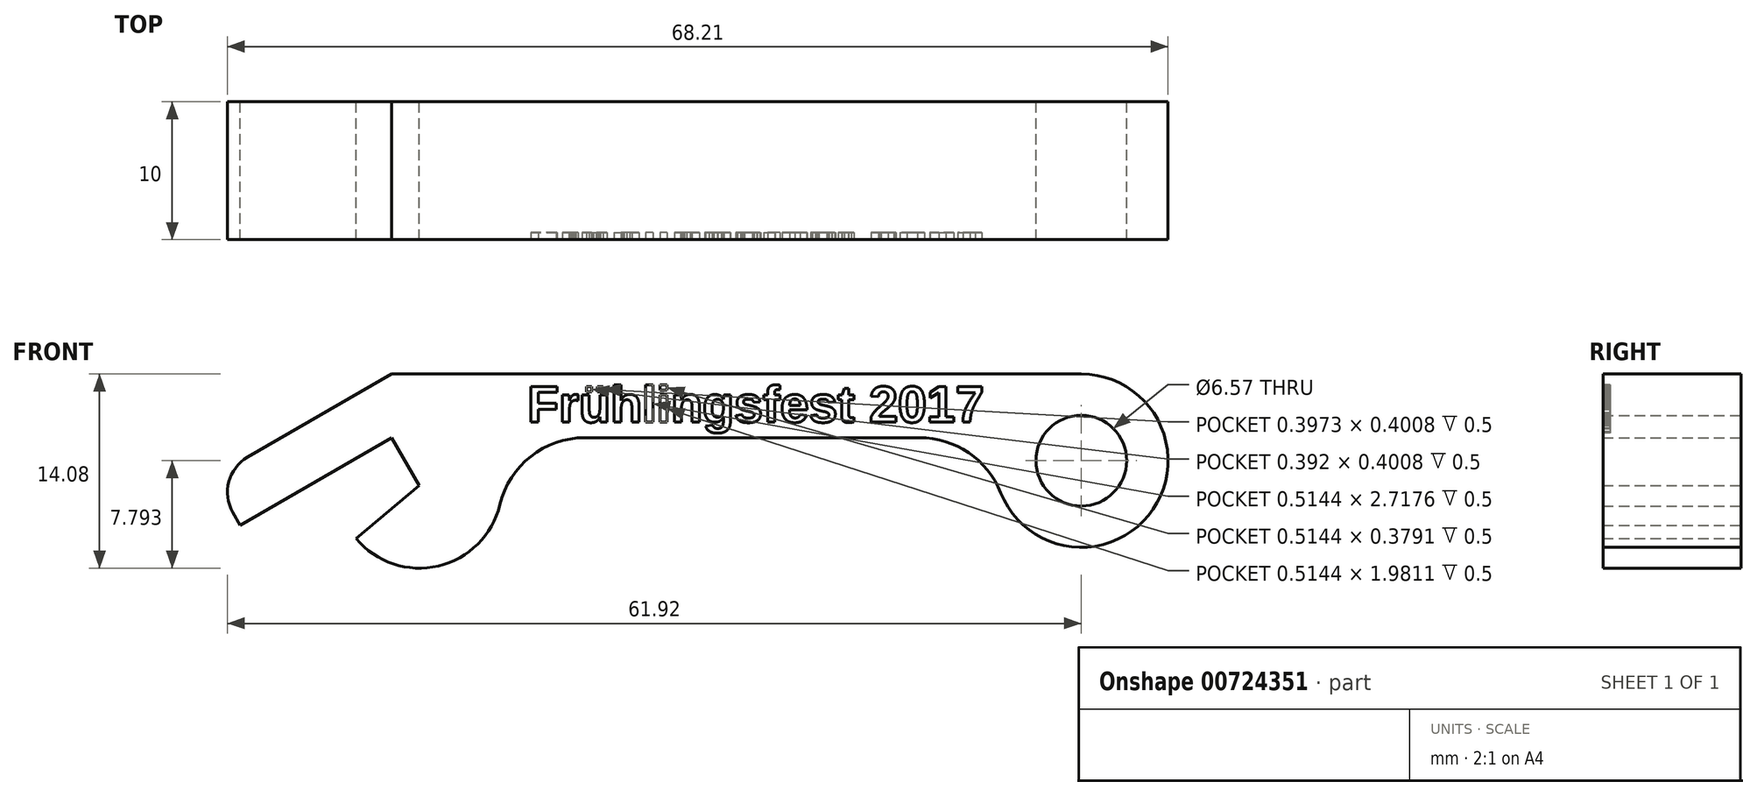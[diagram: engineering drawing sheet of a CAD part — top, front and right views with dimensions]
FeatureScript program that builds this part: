
annotation { "Feature Type Name" : "Feature", "Feature Type Description" : "" }
export const myFeature = defineFeature(function(context is Context, id is Id, definition is map)
    precondition{}
    {
        {
            var Q0;
            Q0=qCreatedBy(makeId("Front.planeOp"),FACE);
            var sketch = newSketch(context, id + "F0", { "sketchPlane" : qUnion([Q0])});
            skLineSegment(sketch, "E0", {"start": v(0, 0) * mm, "end": v(50, 0) * mm});
            skLineSegment(sketch, "E1", {"start": v(50, 0) * mm, "end": v(0, 0) * mm});
            skLineSegment(sketch, "E2", {"start": v(-10.46, -6.04) * mm, "end": v(0, 0) * mm});
            skLineSegment(sketch, "E3", {"start": v(-11.53, -10.03) * mm, "end": v(-11, -10.96) * mm});
            skLineSegment(sketch, "E4", {"start": v(-11, -10.96) * mm, "end": v(0, -4.62) * mm});
            skArc(sketch, "E5", {"start": v(50, 0) * mm, "mid": v(55.2, -9.81) * mm, "end": v(44.16, -8.62) * mm});
            skLineSegment(sketch, "E6", {"start": v(0, -4.62) * mm, "end": v(2, -8.08) * mm});
            skLineSegment(sketch, "E7", {"start": v(2, -8.08) * mm, "end": v(-2.6, -11.94) * mm});
            skArc(sketch, "E8", {"start": v(-2.6, -11.94) * mm, "mid": v(3.37, -13.92) * mm, "end": v(7.83, -9.48) * mm});
            skLineSegment(sketch, "E9", {"start": v(14, -4.62) * mm, "end": v(38.26, -4.62) * mm});
            skCircle(sketch, "E10", {"center": v(50, -6.29) * mm, "radius": 3.29 * mm});
            skPoint(sketch, "E11.visualSharp", {"position": v(-13, -7.5) * mm});
            skArc(sketch, "E11.filletArc", {"start": v(-10.46, -6.04) * mm, "mid": v(-11.82, -7.81) * mm, "end": v(-11.53, -10.03) * mm});
            skPoint(sketch, "E12.visualSharp", {"position": v(6.9, -4.62) * mm});
            skArc(sketch, "E12.filletArc", {"start": v(14, -4.62) * mm, "mid": v(10.08, -5.98) * mm, "end": v(7.83, -9.48) * mm});
            skPoint(sketch, "E13.visualSharp", {"position": v(43.94, -4.62) * mm});
            skArc(sketch, "E13.filletArc", {"start": v(44.16, -8.62) * mm, "mid": v(41.83, -5.71) * mm, "end": v(38.26, -4.62) * mm});
            skSolve(sketch);
        }
        {
            var Q0;
            Q0=qSketchRegion(id+"F0",true);
            extrude(context, id + "F1", {"entities" : qUnion([Q0]), "depth" : 10 * mm, "offsetDistance" : 25.4 * mm});
        }
        {
            var Q0;
            Q0=makeQuery(id+"F1.opExtrude","CAP_FACE",FACE,{"disambiguationData":[OSD([sQuery(id+"F0.wireOp",EDGE,"E1"),sQuery(id+"F0.wireOp",EDGE,"E2"),sQuery(id+"F0.wireOp",EDGE,"E3"),sQuery(id+"F0.wireOp",EDGE,"E4"),sQuery(id+"F0.wireOp",EDGE,"E5"),sQuery(id+"F0.wireOp",EDGE,"E6"),sQuery(id+"F0.wireOp",EDGE,"E7"),sQuery(id+"F0.wireOp",EDGE,"E8"),sQuery(id+"F0.wireOp",EDGE,"E9"),sQuery(id+"F0.wireOp",EDGE,"E10"),sQuery(id+"F0.wireOp",EDGE,"E11.filletArc"),sQuery(id+"F0.wireOp",EDGE,"E12.filletArc"),sQuery(id+"F0.wireOp",EDGE,"E13.filletArc")])],"isStart":false});
            var sketch = newSketch(context, id + "F2", { "sketchPlane" : qUnion([Q0])});
            skText(sketch, "E14", { "text": "Frühlingsfest 2017", "fontName": "Arimo-Bold.ttf"});
            const initialGuessF2  = {"E14": [0.00982, -0.0035, 1, 0, 0.0027]};
            skSetInitialGuess(sketch, initialGuessF2);
            skSolve(sketch);
        }
        {
            var Q0;
            Q0 = qSketchRegion(id + "F2", true);
            extrude(context, id + "F3", {"entities" : qUnion([Q0]), "operationType" : NewBodyOperationType.REMOVE, "oppositeDirection" : true, "depth" : 0.5 * mm, "offsetDistance" : 25.4 * mm});
        }
    });
